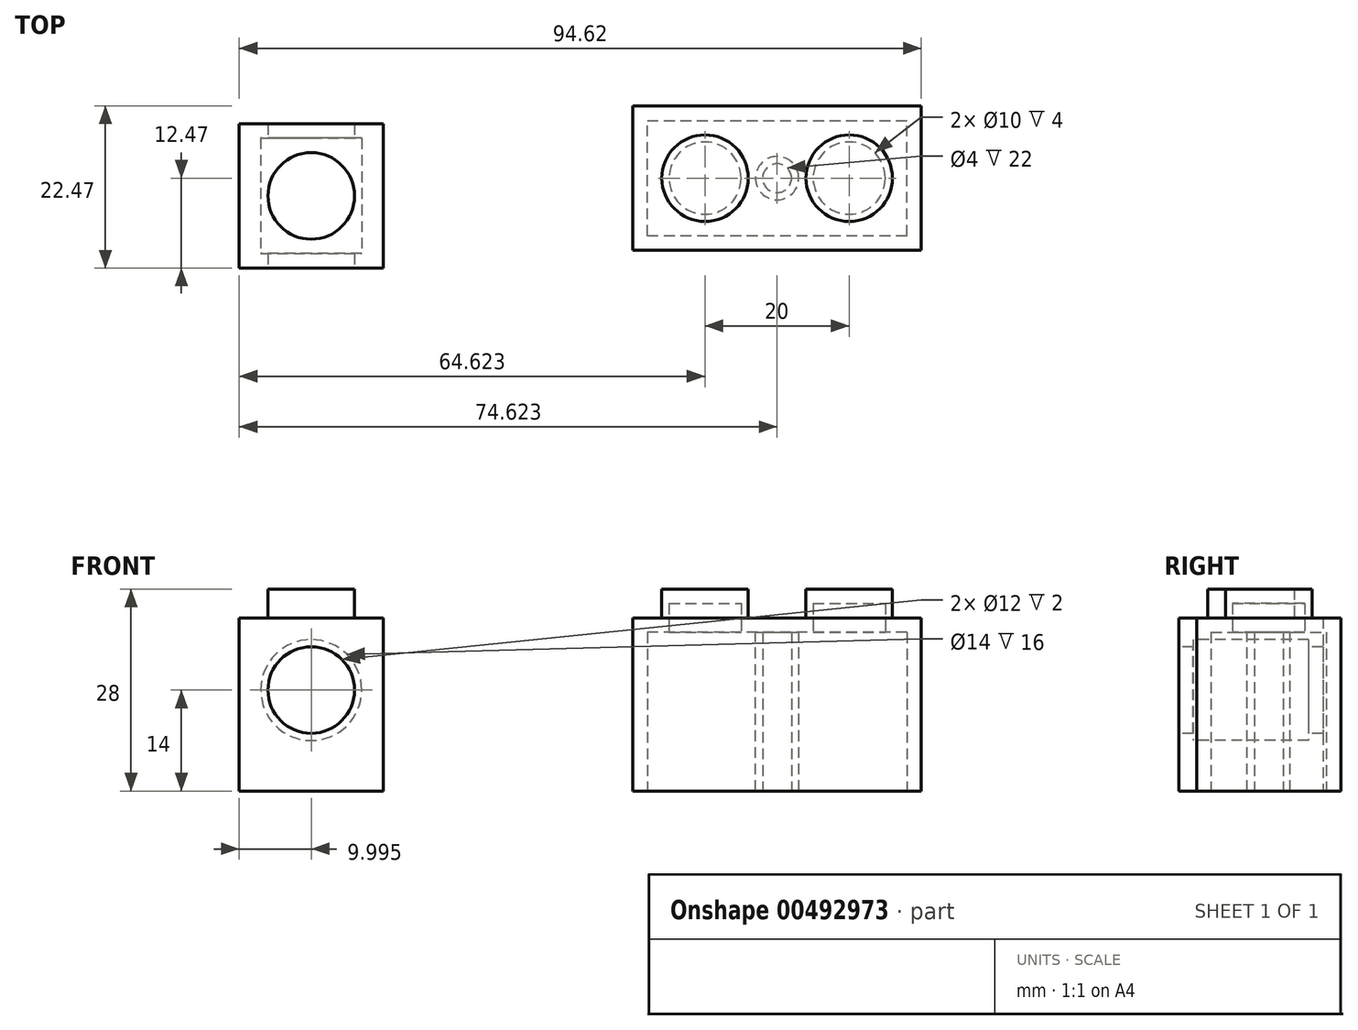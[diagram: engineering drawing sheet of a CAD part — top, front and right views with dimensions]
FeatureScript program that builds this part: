
annotation { "Feature Type Name" : "Feature", "Feature Type Description" : "" }
export const myFeature = defineFeature(function(context is Context, id is Id, definition is map)
    precondition{}
    {
        {
            var Q0;
            Q0=qCreatedBy(makeId("Top.planeOp"),FACE);
            var sketch = newSketch(context, id + "F0", { "sketchPlane" : qUnion([Q0])});
            skLineSegment(sketch, "E0.bottom", {"start": v(-124.05, -59.9) * mm, "end": v(-84.05, -59.9) * mm});
            skLineSegment(sketch, "E0.top", {"start": v(-124.05, -79.9) * mm, "end": v(-84.05, -79.9) * mm});
            skLineSegment(sketch, "E0.left", {"start": v(-124.05, -59.9) * mm, "end": v(-124.05, -79.9) * mm});
            skLineSegment(sketch, "E0.right", {"start": v(-84.05, -59.9) * mm, "end": v(-84.05, -79.9) * mm});
            skSolve(sketch);
        }
        {
            var Q0;
            Q0=makeQuery(id+"F0.imprint","IMPRINT",FACE,{"disambiguationData":[TD([[makeQuery(id+"F0.imprint","IMPRINT",EDGE,{"derivedFrom":sQuery(id+"F0.wireOp",EDGE,"E0.bottom")}),-1.0]])]});
            extrude(context, id + "F1", {"entities" : qUnion([Q0]), "depth" : 24 * mm});
        }
        {
            var Q0;
            Q0=makeQuery(id+"F1.opExtrude","CAP_FACE",FACE,{"disambiguationData":[OSD([sQuery(id+"F0.wireOp",EDGE,"E0.bottom"),sQuery(id+"F0.wireOp",EDGE,"E0.top"),sQuery(id+"F0.wireOp",EDGE,"E0.left"),sQuery(id+"F0.wireOp",EDGE,"E0.right")])],"isStart":false});
            var sketch = newSketch(context, id + "F2", { "sketchPlane" : qUnion([Q0])});
            skLineSegment(sketch, "E1", {"start": v(-124.05, -69.9) * mm, "end": v(-114.05, -69.9) * mm});
            skCircle(sketch, "E2", {"center": v(-114.05, -69.9) * mm, "radius": 6 * mm});
            skLineSegment(sketch, "E3", {"start": v(-84.05, -69.9) * mm, "end": v(-94.05, -69.9) * mm});
            skCircle(sketch, "E4", {"center": v(-94.05, -69.9) * mm, "radius": 6 * mm});
            skSolve(sketch);
        }
        {
            var Q0;
            Q0 = qSketchRegion(id + "F2", true);
            extrude(context, id + "F3", {"entities" : qUnion([Q0]), "operationType" : NewBodyOperationType.ADD, "depth" : 4 * mm});
        }
        {
            var Q0;
            Q0=makeQuery(id+"F1.opExtrude","CAP_FACE",FACE,{"disambiguationData":[OSD([sQuery(id+"F0.wireOp",EDGE,"E0.bottom"),sQuery(id+"F0.wireOp",EDGE,"E0.top"),sQuery(id+"F0.wireOp",EDGE,"E0.left"),sQuery(id+"F0.wireOp",EDGE,"E0.right")])],"isStart":true});
            var sketch = newSketch(context, id + "F4", { "sketchPlane" : qUnion([Q0])});
            skLineSegment(sketch, "E5", {"start": v(-124.05, 69.9) * mm, "end": v(-122.05, 69.9) * mm});
            skLineSegment(sketch, "E6", {"start": v(-84.05, 69.9) * mm, "end": v(-86.05, 69.9) * mm});
            skLineSegment(sketch, "E7", {"start": v(-104.05, 59.9) * mm, "end": v(-104.05, 61.9) * mm});
            skLineSegment(sketch, "E8", {"start": v(-104.05, 79.9) * mm, "end": v(-104.05, 77.9) * mm});
            skPoint(sketch, "E8.endSnap0", {"position": v(-104.05, 79.9) * mm});
            skLineSegment(sketch, "E9.bottom", {"start": v(-122.05, 69.9) * mm, "end": v(-104.05, 69.9) * mm});
            skLineSegment(sketch, "E9.top", {"start": v(-122.05, 61.9) * mm, "end": v(-104.05, 61.9) * mm});
            skLineSegment(sketch, "E9.left", {"start": v(-122.05, 69.9) * mm, "end": v(-122.05, 61.9) * mm});
            skLineSegment(sketch, "E9.right", {"start": v(-104.05, 69.9) * mm, "end": v(-104.05, 61.9) * mm});
            skLineSegment(sketch, "E10.bottom", {"start": v(-104.05, 77.9) * mm, "end": v(-86.05, 77.9) * mm});
            skLineSegment(sketch, "E10.top", {"start": v(-104.05, 69.9) * mm, "end": v(-86.05, 69.9) * mm});
            skLineSegment(sketch, "E10.left", {"start": v(-104.05, 77.9) * mm, "end": v(-104.05, 69.9) * mm});
            skLineSegment(sketch, "E10.right", {"start": v(-86.05, 77.9) * mm, "end": v(-86.05, 69.9) * mm});
            skLineSegment(sketch, "E11.bottom", {"start": v(-86.05, 69.9) * mm, "end": v(-104.05, 69.9) * mm});
            skLineSegment(sketch, "E11.top", {"start": v(-86.05, 61.9) * mm, "end": v(-104.05, 61.9) * mm});
            skLineSegment(sketch, "E11.left", {"start": v(-86.05, 69.9) * mm, "end": v(-86.05, 61.9) * mm});
            skLineSegment(sketch, "E12.bottom", {"start": v(-104.05, 69.9) * mm, "end": v(-122.05, 69.9) * mm});
            skLineSegment(sketch, "E12.top", {"start": v(-104.05, 77.9) * mm, "end": v(-122.05, 77.9) * mm});
            skLineSegment(sketch, "E12.left", {"start": v(-104.05, 69.9) * mm, "end": v(-104.05, 77.9) * mm});
            skLineSegment(sketch, "E12.right", {"start": v(-122.05, 69.9) * mm, "end": v(-122.05, 77.9) * mm});
            skSolve(sketch);
        }
        {
            var Q0;
            Q0 = qSketchRegion(id + "F4", true);
            extrude(context, id + "F5", {"entities" : qUnion([Q0]), "operationType" : NewBodyOperationType.REMOVE, "oppositeDirection" : true, "depth" : 22 * mm});
        }
        {
            var Q0;
            Q0=makeQuery(id+"F5.boolean.opBoolean","COPY",FACE,{"derivedFrom":makeQuery(id+"F5.opExtrude","CAP_FACE",FACE,{"disambiguationData":[OSD([sQuery(id+"F4.wireOp",EDGE,"E9.top"),sQuery(id+"F4.wireOp",EDGE,"E9.left"),sQuery(id+"F4.wireOp",EDGE,"E10.bottom"),sQuery(id+"F4.wireOp",EDGE,"E10.right"),sQuery(id+"F4.wireOp",EDGE,"E11.top"),sQuery(id+"F4.wireOp",EDGE,"E11.left"),sQuery(id+"F4.wireOp",EDGE,"E12.top"),sQuery(id+"F4.wireOp",EDGE,"E12.right")])],"isStart":false})});
            var sketch = newSketch(context, id + "F6", { "sketchPlane" : qUnion([Q0])});
            skPoint(sketch, "E13", {"position": v(-107.77, -49.68) * mm});
            skLineSegment(sketch, "E14", {"start": v(-122.05, 69.9) * mm, "end": v(-114.05, 69.9) * mm});
            skCircle(sketch, "E15", {"center": v(-114.05, 69.9) * mm, "radius": 5 * mm});
            skLineSegment(sketch, "E16", {"start": v(-86.05, 69.9) * mm, "end": v(-94.05, 69.9) * mm});
            skCircle(sketch, "E17", {"center": v(-94.05, 69.9) * mm, "radius": 5 * mm});
            skSolve(sketch);
        }
        {
            var Q0;
            Q0=makeQuery(id+"F6.imprint","IMPRINT",FACE,{"disambiguationData":[TD([[makeQuery(id+"F6.imprint","IMPRINT",EDGE,{"derivedFrom":sQuery(id+"F6.wireOp",EDGE,"E17")}),1.0]])]});
            var Q1;
            Q1=makeQuery(id+"F6.imprint","IMPRINT",FACE,{"disambiguationData":[TD([[makeQuery(id+"F6.imprint","IMPRINT",EDGE,{"derivedFrom":sQuery(id+"F6.wireOp",EDGE,"E15")}),1.0]])]});
            extrude(context, id + "F7", {"entities" : qUnion([Q0, Q1]), "operationType" : NewBodyOperationType.REMOVE, "oppositeDirection" : true, "depth" : 4 * mm});
        }
        {
            var Q0;
            Q0=makeQuery(id+"F5.boolean.opBoolean","COPY",FACE,{"derivedFrom":makeQuery(id+"F5.opExtrude","CAP_FACE",FACE,{"disambiguationData":[OSD([sQuery(id+"F4.wireOp",EDGE,"E9.top"),sQuery(id+"F4.wireOp",EDGE,"E9.left"),sQuery(id+"F4.wireOp",EDGE,"E10.bottom"),sQuery(id+"F4.wireOp",EDGE,"E10.right"),sQuery(id+"F4.wireOp",EDGE,"E11.top"),sQuery(id+"F4.wireOp",EDGE,"E11.left"),sQuery(id+"F4.wireOp",EDGE,"E12.top"),sQuery(id+"F4.wireOp",EDGE,"E12.right")])],"isStart":false})});
            var sketch = newSketch(context, id + "F8", { "sketchPlane" : qUnion([Q0])});
            skLineSegment(sketch, "E18", {"start": v(-114.05, 69.9) * mm, "end": v(-104.05, 69.9) * mm});
            skCircle(sketch, "E19", {"center": v(-104.05, 69.9) * mm, "radius": 3 * mm});
            skSolve(sketch);
        }
        {
            var Q0;
            Q0 = qSketchRegion(id + "F8", true);
            extrude(context, id + "F9", {"entities" : qUnion([Q0]), "operationType" : NewBodyOperationType.ADD, "depth" : 22 * mm});
        }
        {
            var Q0;
            Q0=makeQuery(id+"F9.opExtrude","CAP_FACE",FACE,{"disambiguationData":[OSD([sQuery(id+"F8.wireOp",EDGE,"E19")])],"isStart":false});
            var sketch = newSketch(context, id + "F10", { "sketchPlane" : qUnion([Q0])});
            skCircle(sketch, "E20", {"center": v(-104.05, 69.9) * mm, "radius": 2 * mm});
            skSolve(sketch);
        }
        {
            var Q0;
            Q0=makeQuery(id+"F10.imprint","IMPRINT",FACE,{"disambiguationData":[TD([[makeQuery(id+"F10.imprint","IMPRINT",EDGE,{"derivedFrom":sQuery(id+"F10.wireOp",EDGE,"E20")}),1.0]])]});
            extrude(context, id + "F11", {"entities" : qUnion([Q0]), "operationType" : NewBodyOperationType.REMOVE, "oppositeDirection" : true, "depth" : 22 * mm});
        }
        {
            var Q0;
            Q0=qCreatedBy(makeId("Top.planeOp"),FACE);
            var sketch = newSketch(context, id + "F12", { "sketchPlane" : qUnion([Q0])});
            skLineSegment(sketch, "E21.bottom", {"start": v(-178.67, -62.37) * mm, "end": v(-158.67, -62.37) * mm});
            skLineSegment(sketch, "E21.top", {"start": v(-178.67, -82.37) * mm, "end": v(-158.67, -82.37) * mm});
            skLineSegment(sketch, "E21.left", {"start": v(-178.67, -62.37) * mm, "end": v(-178.67, -82.37) * mm});
            skLineSegment(sketch, "E21.right", {"start": v(-158.67, -62.37) * mm, "end": v(-158.67, -82.37) * mm});
            skSolve(sketch);
        }
        {
            var Q0;
            Q0=makeQuery(id+"F12.imprint","IMPRINT",FACE,{"disambiguationData":[TD([[makeQuery(id+"F12.imprint","IMPRINT",EDGE,{"derivedFrom":sQuery(id+"F12.wireOp",EDGE,"E21.bottom")}),-1.0]])]});
            extrude(context, id + "F13", {"entities" : qUnion([Q0]), "depth" : 24 * mm});
        }
        {
            var Q0;
            Q0=makeQuery(id+"F13.opExtrude","CAP_FACE",FACE,{"disambiguationData":[OSD([sQuery(id+"F12.wireOp",EDGE,"E21.bottom"),sQuery(id+"F12.wireOp",EDGE,"E21.top"),sQuery(id+"F12.wireOp",EDGE,"E21.left"),sQuery(id+"F12.wireOp",EDGE,"E21.right")])],"isStart":false});
            var sketch = newSketch(context, id + "F14", { "sketchPlane" : qUnion([Q0])});
            skLineSegment(sketch, "E22", {"start": v(-178.67, -72.37) * mm, "end": v(-168.67, -72.37) * mm});
            skCircle(sketch, "E23", {"center": v(-168.67, -72.37) * mm, "radius": 6 * mm});
            skSolve(sketch);
        }
        {
            var Q0;
            Q0=makeQuery(id+"F14.imprint","IMPRINT",FACE,{"disambiguationData":[TD([[makeQuery(id+"F14.imprint","IMPRINT",EDGE,{"derivedFrom":sQuery(id+"F14.wireOp",EDGE,"E23")}),1.0]])]});
            extrude(context, id + "F15", {"entities" : qUnion([Q0]), "operationType" : NewBodyOperationType.ADD, "depth" : 4 * mm});
        }
        {
            var Q0;
            Q0=makeQuery(id+"F13.opExtrude","CAP_FACE",FACE,{"disambiguationData":[OSD([sQuery(id+"F12.wireOp",EDGE,"E21.bottom"),sQuery(id+"F12.wireOp",EDGE,"E21.top"),sQuery(id+"F12.wireOp",EDGE,"E21.left"),sQuery(id+"F12.wireOp",EDGE,"E21.right")])],"isStart":true});
            var sketch = newSketch(context, id + "F16", { "sketchPlane" : qUnion([Q0])});
            skLineSegment(sketch, "E24", {"start": v(-178.67, 72.37) * mm, "end": v(-176.67, 72.37) * mm});
            skLineSegment(sketch, "E25", {"start": v(-158.67, 72.37) * mm, "end": v(-160.67, 72.37) * mm});
            skLineSegment(sketch, "E26", {"start": v(-168.67, 82.37) * mm, "end": v(-168.67, 80.37) * mm});
            skLineSegment(sketch, "E27.bottom", {"start": v(-176.67, 72.37) * mm, "end": v(-168.67, 72.37) * mm});
            skLineSegment(sketch, "E27.top", {"start": v(-176.67, 80.37) * mm, "end": v(-168.67, 80.37) * mm});
            skLineSegment(sketch, "E27.left", {"start": v(-176.67, 72.37) * mm, "end": v(-176.67, 80.37) * mm});
            skLineSegment(sketch, "E27.right", {"start": v(-168.67, 72.37) * mm, "end": v(-168.67, 80.37) * mm});
            skLineSegment(sketch, "E28.bottom", {"start": v(-168.67, 80.37) * mm, "end": v(-160.67, 80.37) * mm});
            skLineSegment(sketch, "E28.top", {"start": v(-168.67, 72.37) * mm, "end": v(-160.67, 72.37) * mm});
            skLineSegment(sketch, "E28.left", {"start": v(-168.67, 80.37) * mm, "end": v(-168.67, 72.37) * mm});
            skLineSegment(sketch, "E28.right", {"start": v(-160.67, 80.37) * mm, "end": v(-160.67, 72.37) * mm});
            skLineSegment(sketch, "E29", {"start": v(-168.67, 62.37) * mm, "end": v(-168.67, 64.37) * mm});
            skLineSegment(sketch, "E30.top", {"start": v(-176.67, 64.37) * mm, "end": v(-168.67, 64.37) * mm});
            skLineSegment(sketch, "E30.left", {"start": v(-176.67, 72.37) * mm, "end": v(-176.67, 64.37) * mm});
            skLineSegment(sketch, "E30.right", {"start": v(-168.67, 72.37) * mm, "end": v(-168.67, 64.37) * mm});
            skLineSegment(sketch, "E31.bottom", {"start": v(-168.67, 64.37) * mm, "end": v(-160.67, 64.37) * mm});
            skLineSegment(sketch, "E31.left", {"start": v(-168.67, 64.37) * mm, "end": v(-168.67, 72.37) * mm});
            skLineSegment(sketch, "E31.right", {"start": v(-160.67, 64.37) * mm, "end": v(-160.67, 72.37) * mm});
            skSolve(sketch);
        }
        {
            var Q0;
            Q0 = qSketchRegion(id + "F16", true);
            extrude(context, id + "F17", {"entities" : qUnion([Q0]), "operationType" : NewBodyOperationType.REMOVE, "oppositeDirection" : true, "depth" : 22 * mm});
        }
        {
            var Q0;
            Q0=makeQuery(id+"F13.opExtrude","SWEPT_FACE",FACE,{"disambiguationData":[OSD([sQuery(id+"F12.wireOp",EDGE,"E21.top")])]});
            var sketch = newSketch(context, id + "F18", { "sketchPlane" : qUnion([Q0])});
            skLineSegment(sketch, "E32", {"start": v(-178.67, 12) * mm, "end": v(-158.67, 12) * mm});
            skLineSegment(sketch, "E33", {"start": v(-168.67, 12) * mm, "end": v(-168.67, 14) * mm});
            skPoint(sketch, "E33.endSnap0", {"position": v(-168.67, 12) * mm});
            skCircle(sketch, "E34", {"center": v(-168.67, 14) * mm, "radius": 7 * mm});
            skCircle(sketch, "E35", {"center": v(-168.67, 14) * mm, "radius": 6 * mm});
            skSolve(sketch);
        }
        {
            var Q0;
            {var subQ0=sQuery(id+"F18.wireOp",EDGE,"E34");var subQ1=sQuery(id+"F18.wireOp",EDGE,"E32");var subQ2=makeQuery(id+"F18.imprint","INTERSECT",VERTEX,{"disambiguationData":[OD(0.0)],"derivedFrom":[subQ1,subQ0]});Q0=makeQuery(id+"F18.imprint","IMPRINT",FACE,{"disambiguationData":[TD([[makeQuery(id+"F18.imprint","IMPRINT",EDGE,{"disambiguationData":[TD([[subQ2,-1.0]])],"derivedFrom":subQ1}),-1.0]])]});}
            var Q1;
            {var subQ0=sQuery(id+"F18.wireOp",EDGE,"E34");var subQ1=sQuery(id+"F18.wireOp",EDGE,"E32");var subQ2=makeQuery(id+"F18.imprint","INTERSECT",VERTEX,{"disambiguationData":[OD(0.0)],"derivedFrom":[subQ1,subQ0]});Q1=makeQuery(id+"F18.imprint","IMPRINT",FACE,{"disambiguationData":[TD([[makeQuery(id+"F18.imprint","IMPRINT",EDGE,{"disambiguationData":[TD([[subQ2,-1.0]])],"derivedFrom":subQ1}),1.0]])]});}
            extrude(context, id + "F19", {"entities" : qUnion([Q0, Q1]), "operationType" : NewBodyOperationType.ADD, "oppositeDirection" : true, "depth" : 20 * mm});
        }
        {
            var Q0;
            {var subQ0=sQuery(id+"F18.wireOp",EDGE,"E32");var subQ1=makeQuery(id+"F18.imprint","IMPRINT",VERTEX,{"derivedFrom":subQ0});Q0=makeQuery(id+"F18.imprint","IMPRINT",FACE,{"disambiguationData":[TD([[makeQuery(id+"F18.imprint","IMPRINT",EDGE,{"disambiguationData":[TD([[subQ1,1.0]])],"derivedFrom":subQ0}),1.0]])]});}
            var Q1;
            {var subQ0=sQuery(id+"F18.wireOp",EDGE,"E32");var subQ1=makeQuery(id+"F18.imprint","IMPRINT",VERTEX,{"derivedFrom":subQ0});Q1=makeQuery(id+"F18.imprint","IMPRINT",FACE,{"disambiguationData":[TD([[makeQuery(id+"F18.imprint","IMPRINT",EDGE,{"disambiguationData":[TD([[subQ1,1.0]])],"derivedFrom":subQ0}),-1.0]])]});}
            extrude(context, id + "F20", {"entities" : qUnion([Q0, Q1]), "operationType" : NewBodyOperationType.REMOVE, "oppositeDirection" : true, "depth" : 25 * mm});
        }
    });
